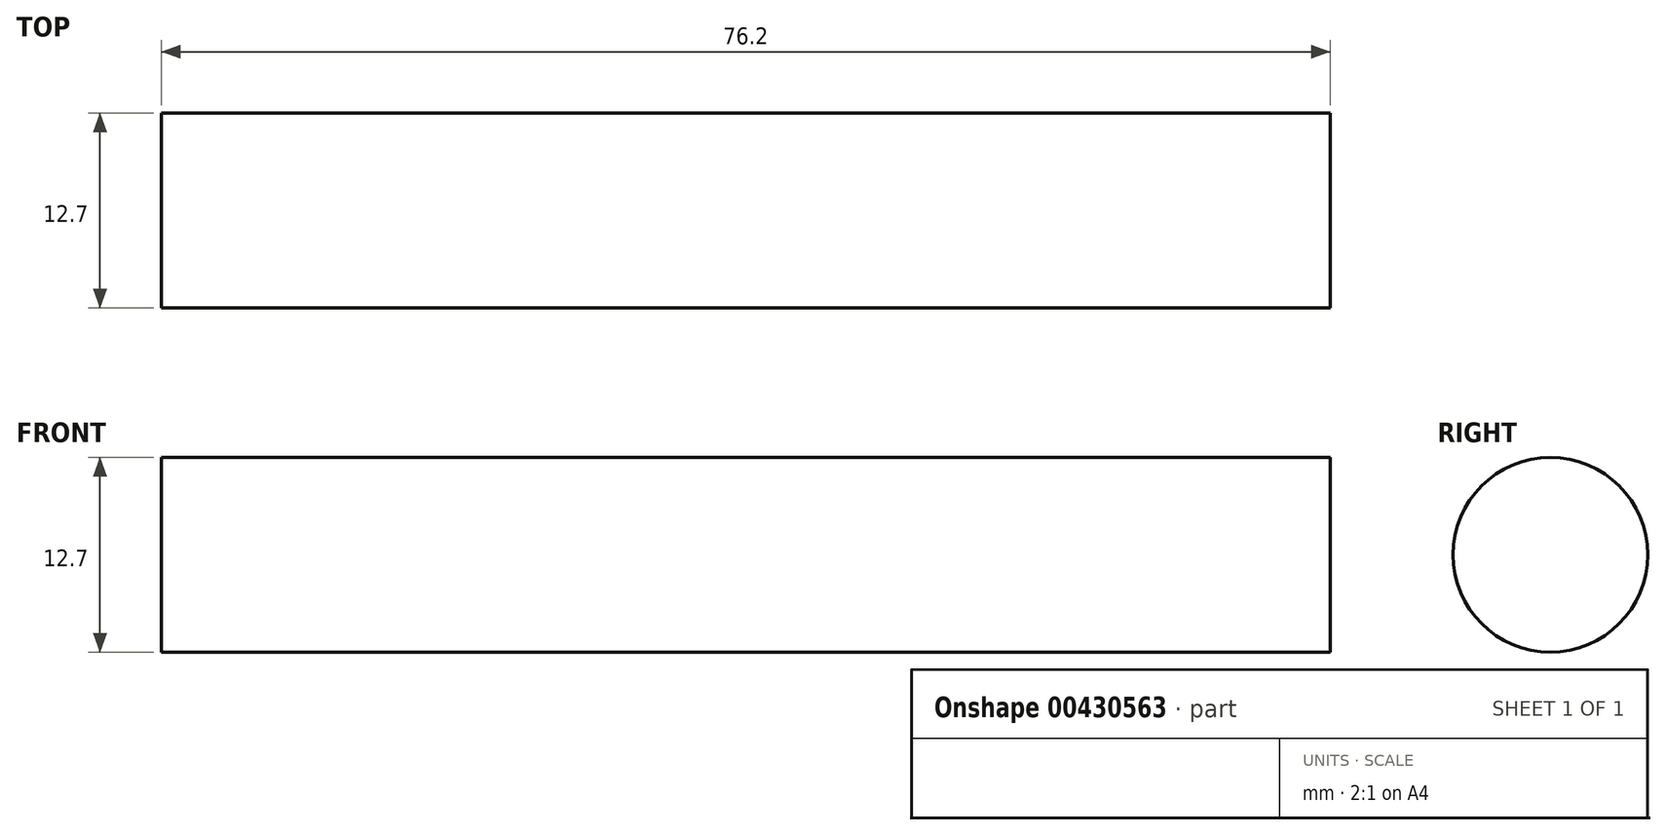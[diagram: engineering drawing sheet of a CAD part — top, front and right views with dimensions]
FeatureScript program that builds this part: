
annotation { "Feature Type Name" : "Feature", "Feature Type Description" : "" }
export const myFeature = defineFeature(function(context is Context, id is Id, definition is map)
    precondition{}
    {
        {
            var Q0;
            Q0=qCreatedBy(makeId("Right.planeOp"),FACE);
            var sketch = newSketch(context, id + "F0", { "sketchPlane" : qUnion([Q0])});
            skCircle(sketch, "E0", {"center": v(0, 1.2) * mm, "radius": 6.35 * mm});
            skSolve(sketch);
        }
        {
            var Q0;
            Q0=makeQuery(id+"F0.imprint","IMPRINT",FACE,{"disambiguationData":[TD([[makeQuery(id+"F0.imprint","IMPRINT",EDGE,{"derivedFrom":sQuery(id+"F0.wireOp",EDGE,"E0")}),1.0]])]});
            extrude(context, id + "F1", {"entities" : qUnion([Q0]), "depth" : 76.2 * mm});
        }
    });
